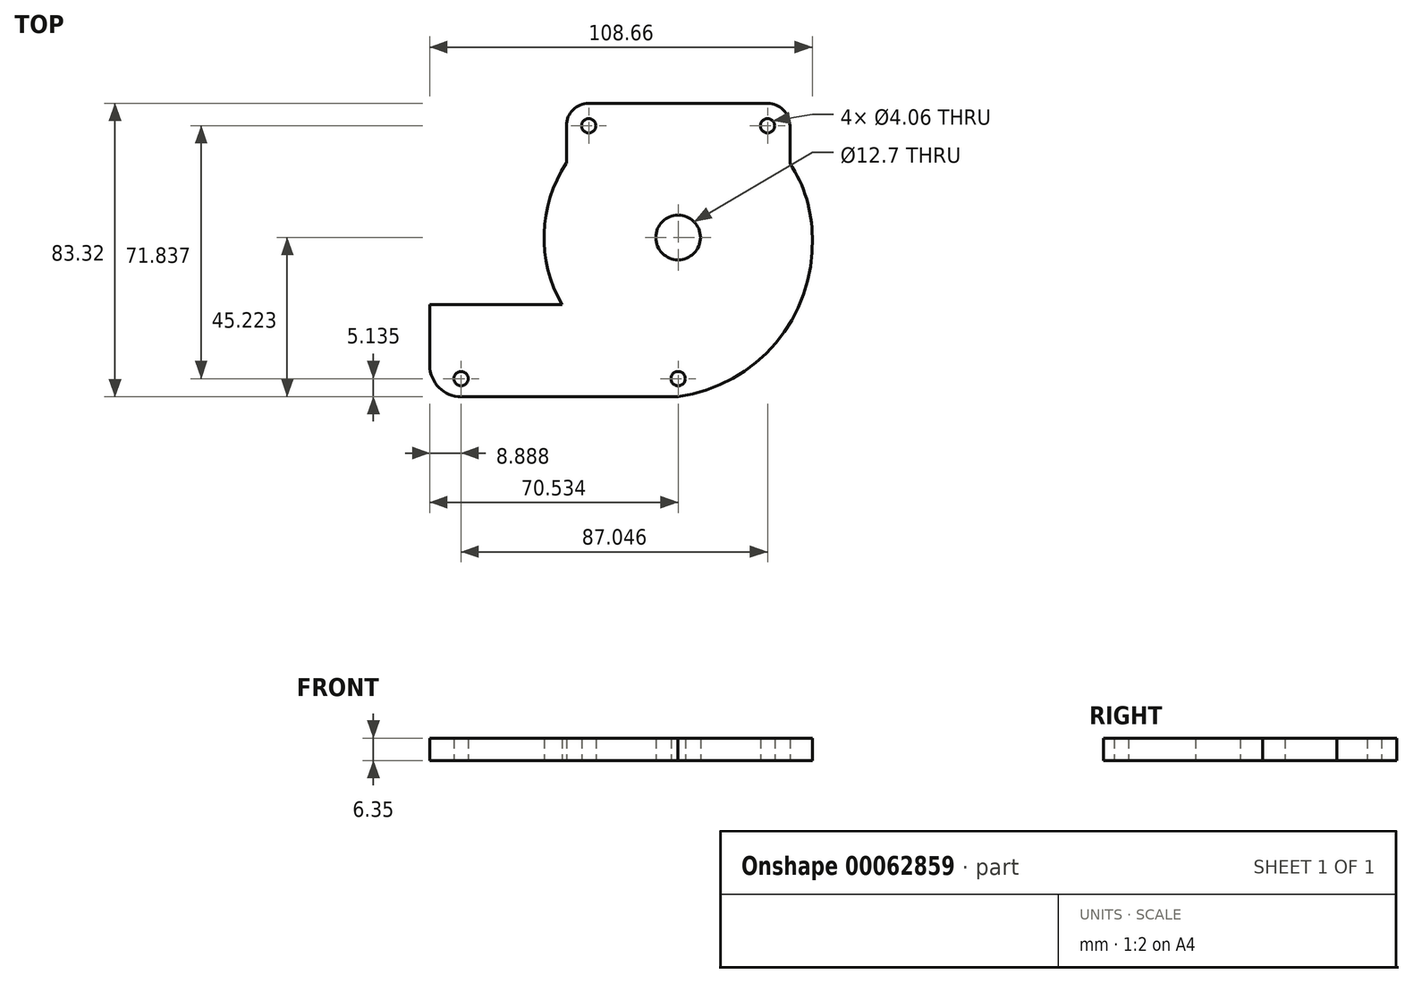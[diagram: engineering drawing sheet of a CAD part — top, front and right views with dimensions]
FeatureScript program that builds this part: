
annotation { "Feature Type Name" : "Feature", "Feature Type Description" : "" }
export const myFeature = defineFeature(function(context is Context, id is Id, definition is map)
    precondition{}
    {
        {
            var Q0;
            Q0=qCreatedBy(makeId("Top.planeOp"),FACE);
            var sketch = newSketch(context, id + "F0", { "sketchPlane" : qUnion([Q0])});
            skArc(sketch, "E0", {"start": v(57.92, 5.8) * mm, "mid": v(56.3, 16.8) * mm, "end": v(51.57, 26.85) * mm});
            skLineSegment(sketch, "E1", {"start": v(-50.71, -25.96) * mm, "end": v(-50.71, -13.26) * mm});
            skLineSegment(sketch, "E2", {"start": v(-50.71, -13.26) * mm, "end": v(-13.17, -13.26) * mm});
            skPoint(sketch, "E3.visualSharp", {"position": v(-50.71, -32.3) * mm});
            skLineSegment(sketch, "E4", {"start": v(19.82, 43.9) * mm, "end": v(-5.58, 43.9) * mm});
            skLineSegment(sketch, "E5", {"start": v(19.82, 43.9) * mm, "end": v(45.22, 43.9) * mm});
            skLineSegment(sketch, "E6", {"start": v(-11.93, 37.54) * mm, "end": v(-11.93, 26.85) * mm});
            skLineSegment(sketch, "E7", {"start": v(51.57, 37.54) * mm, "end": v(51.57, 26.85) * mm});
            skArc(sketch, "E8.trimOffspring", {"start": v(-11.93, 26.85) * mm, "mid": v(-18.26, 6.98) * mm, "end": v(-13.17, -13.26) * mm});
            skPoint(sketch, "E9.visualSharp", {"position": v(-11.93, 43.9) * mm});
            skArc(sketch, "E9.filletArc", {"start": v(-5.58, 43.9) * mm, "mid": v(-10.07, 42.03) * mm, "end": v(-11.93, 37.54) * mm});
            skPoint(sketch, "E10.visualSharp", {"position": v(51.57, 43.9) * mm});
            skArc(sketch, "E10.filletArc", {"start": v(51.57, 37.54) * mm, "mid": v(49.71, 42.03) * mm, "end": v(45.22, 43.9) * mm});
            skArc(sketch, "E11", {"start": v(19.8, -39.43) * mm, "mid": v(47.56, -24.15) * mm, "end": v(57.92, 5.8) * mm});
            skPoint(sketch, "E12.orphan", {"position": v(19.82, -32.3) * mm});
            skLineSegment(sketch, "E13", {"start": v(19.82, -25.96) * mm, "end": v(-50.71, -25.96) * mm});
            skCircle(sketch, "E14", {"center": v(-5.58, 37.54) * mm, "radius": 2.03 * mm});
            skCircle(sketch, "E15", {"center": v(45.22, 37.54) * mm, "radius": 2.03 * mm});
            skLineSegment(sketch, "E16", {"start": v(19.8, -39.43) * mm, "end": v(-41.82, -39.43) * mm});
            skLineSegment(sketch, "E17", {"start": v(-50.71, -30.54) * mm, "end": v(-50.71, -25.96) * mm});
            skPoint(sketch, "E18.visualSharp", {"position": v(-50.71, -39.43) * mm});
            skArc(sketch, "E18.filletArc", {"start": v(-50.71, -30.54) * mm, "mid": v(-48.1, -36.83) * mm, "end": v(-41.82, -39.43) * mm});
            skPoint(sketch, "E19.center.orphan", {"position": v(19.8, -36.26) * mm});
            skCircle(sketch, "E20", {"center": v(19.82, -34.3) * mm, "radius": 2.03 * mm});
            skLineSegment(sketch, "E21", {"start": v(19.82, -34.3) * mm, "end": v(-41.82, -34.3) * mm});
            skCircle(sketch, "E22", {"center": v(-41.82, -34.3) * mm, "radius": 2.03 * mm});
            skCircle(sketch, "E23", {"center": v(19.82, 5.8) * mm, "radius": 6.35 * mm});
            skSolve(sketch);
        }
        {
            var Q0;
            Q0 = qSketchRegion(id + "F0", true);
            extrude(context, id + "F1", {"entities" : qUnion([Q0]), "depth" : 6.35 * mm});
        }
    });
